# Revit family: Step_Kattsafe_Double
name_source: partatom
category: Specialty Equipment
units: mm (PartAtom-declared; Revit-internal decimal feet)

## family parameters
Always vertical = Yes
Cut with Voids When Loaded = No
Enable Cutting in Views = No
Maintain Annotation Orientation = No
OmniClass Number = 23.17.23.15
Part Type = Normal
Room Calculation Point = No
Round Connector Dimension = Use Diameter
Shared = No
Work Plane-Based = No

## types (2) — shared parameters
Assembly Code = E1090100
Description = Kattsafe steps provide safe and easy access to varying heights including roof areas, service platforms and other elevated areas where frequent access is required. Manufactured to Australian Standard AS/NZS 1657:2018 which ensures a high level of safety and confidence for maintenance personnel. Available in single and double configurations
ElementType = Ladder
Export Type to IFC As = IfcBuildingElementProxy
IfcExportAs = IfcBuildingElementProxy
IfcExportType = USERDEFINED
Manufacturer = Kattsafe®
ManufacturerOverallHeight = 450 mm  [stored 1.47638 ft]
ManufacturerOverallWidth = 600 mm  [stored 1.9685 ft]
ManufacturerURLProductSpecific = https://kattsafe.com.au
Material = Aluminum_Kattsafe_Satin
ModifiedIssue = 20240430 $
PlatformMaterial = Aluminum_Kattsafe_Mesh_Walkway
Type IFC Predefined Type = USERDEFINED
URL = https://kattsafe.com.au
Uniclass2015Code = Pr_25_30_85_85
Uniclass2015Title = Step-over ladders
Uniclass2015Version = Products v1.23
zero-valued in all types: Default Elevation

## per-type parameters (varying)
| type | BackOffsetValid | ManufacturerOverallDepth | ManufacturerSpecCode | Model | StepOver | TopPlatformDepth | Type Comments |
| Step Up (ST552.300) | 0 mm  [stored 0 ft] | 600 mm  [stored 1.9685 ft] | ST552.300 | ST552.300 | No | 300 mm  [stored 0.984252 ft] | Double Step Up |
| Step Over (ST552.600) | 300 mm  [stored 0.984252 ft] | 1200 mm | ST552.600 | ST552.600 | Yes | 600 mm  [stored 1.9685 ft] | Double Step Over |

note: [stored X ft] marks values corroborated as IEEE doubles in the binary element streams (Revit-internal decimal feet)

## geometry (parser evidence)
native form markers: Sweep x1
no freeform markers — native parametric forms only
